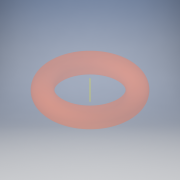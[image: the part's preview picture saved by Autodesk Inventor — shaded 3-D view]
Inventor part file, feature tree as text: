
AUTODESK INVENTOR PART (.ipt)
format: ipt  version: 2019.4 (Build 234330000, 330)  size: 142,336 bytes
history: native  units: in
note: dims shown in document units (in); Inventor stores cm internally (conversion verified against a paired STEP export)
features: sketch x1, other x1, revolve x1
ambient origin geometry x8: Origin, YZ Plane, XZ Plane, XY Plane, X Axis, Y Axis, Z Axis, Center Point
bodies: Body1 (feature_tree)
feature tree (3):
  sketch  "Sketch1"  dims[d0=7.874in d1=15.748in d2=90.0deg]
  other  "Srf1"
  revolve  "RevolutionSrf1"  [1 undecoded]
note: 1 required parameter value undecoded (feature->parameter linkage not recoverable at this tier; creation-order binding heuristic only, values carry confidence <= 0.55)
